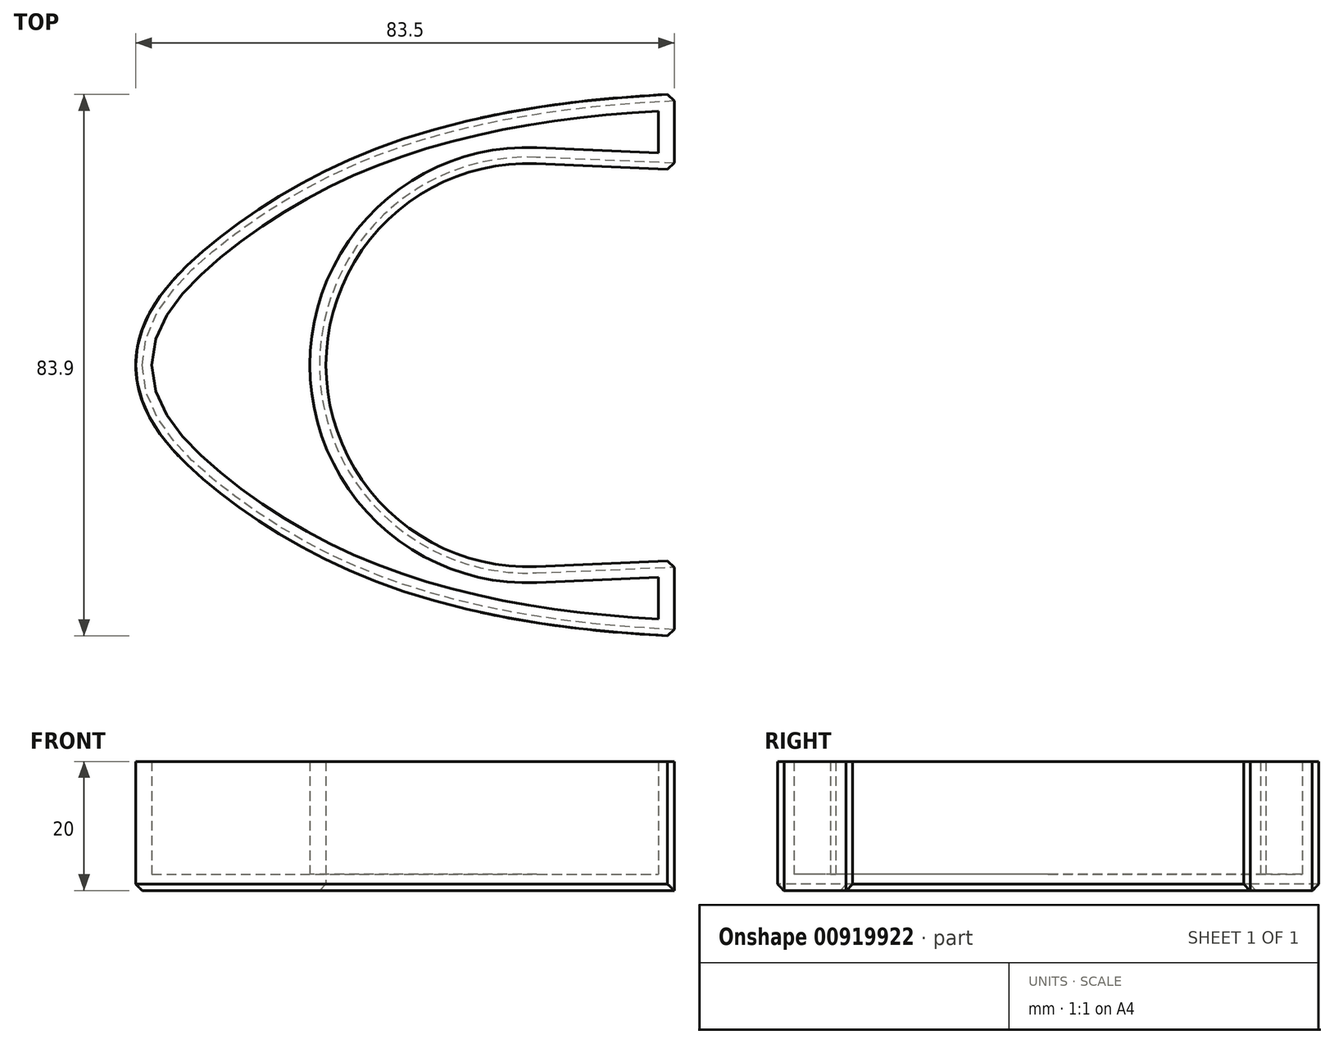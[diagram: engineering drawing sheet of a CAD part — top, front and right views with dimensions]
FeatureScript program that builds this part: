
annotation { "Feature Type Name" : "Feature", "Feature Type Description" : "" }
export const myFeature = defineFeature(function(context is Context, id is Id, definition is map)
    precondition{}
    {
        {
            var Q0;
            Q0=qCreatedBy(makeId("Top.planeOp"),FACE);
            var sketch = newSketch(context, id + "F0", { "sketchPlane" : qUnion([Q0])});
            skCircle(sketch, "E0", {"center": v(0, 0) * mm, "radius": 31.25 * mm});
            skLineSegment(sketch, "E1", {"start": v(22.75, 46.58) * mm, "end": v(22.75, -55.17) * mm, "construction": true});
            skLineSegment(sketch, "E2", {"start": v(1.34, 31.22) * mm, "end": v(22.75, 30.3) * mm});
            skLineSegment(sketch, "E3", {"start": v(1.34, -31.22) * mm, "end": v(22.75, -30.3) * mm});
            skPoint(sketch, "E4", {"position": v(22.75, 0) * mm});
            skFitSpline(sketch, "E5", {"points": [v(-60.75, 0) * mm, v(-45.42, 21.52) * mm, v(22.75, 42) * mm], "startDerivative": vector(0, 66.7) * mm, "endDerivative": vector(171.08, 7.64) * mm});
            skFitSpline(sketch, "E6", {"points": [v(-60.75, 0) * mm, v(-45.42, -21.52) * mm, v(22.75, -42) * mm], "startDerivative": vector(0, -66.7) * mm, "endDerivative": vector(171.08, -7.64) * mm});
            skLineSegment(sketch, "E7", {"start": v(22.75, -30.3) * mm, "end": v(22.75, -42) * mm});
            skLineSegment(sketch, "E8", {"start": v(22.75, 42) * mm, "end": v(22.75, 30.3) * mm});
            skPoint(sketch, "E9", {"position": v(-45.42, 0) * mm});
            skPoint(sketch, "E10", {"position": v(-12.69, 0) * mm});
            skLineSegment(sketch, "E11", {"start": v(-31.25, 0) * mm, "end": v(-31.25, 30.85) * mm, "construction": true});
            skSolve(sketch);
        }
        {
            var Q0;
            {var subQ1=sQuery(id+"F0.wireOp",EDGE,"E2");Q0=makeQuery(id+"F0.imprint","IMPRINT",FACE,{"disambiguationData":[TD([[makeQuery(id+"F0.imprint","IMPRINT",EDGE,{"derivedFrom":subQ1}),1.0]])]});}
            extrude(context, id + "F1", {"entities" : qUnion([Q0]), "depth" : 20 * mm, "offsetDistance" : 25 * mm});
        }
        {
            var Q0;
            Q0=makeQuery(id+"F1.opExtrude","CAP_FACE",FACE,{"disambiguationData":[OSD([sQuery(id+"F0.wireOp",EDGE,"E0"),sQuery(id+"F0.wireOp",EDGE,"E2"),sQuery(id+"F0.wireOp",EDGE,"E3"),sQuery(id+"F0.wireOp",EDGE,"E5"),sQuery(id+"F0.wireOp",EDGE,"E6"),sQuery(id+"F0.wireOp",EDGE,"E7"),sQuery(id+"F0.wireOp",EDGE,"E8")])],"isStart":false});
            shell(context, id + "F2", {"entities" : qUnion([Q0]), "thickness" : 2.5 * mm});
        }
        {
            var Q0;
            Q0=makeQuery(id+"F1.opExtrude","SWEPT_EDGE",EDGE,{"disambiguationData":[OSD([sQuery(id+"F0.wireOp",EDGE,"E6"),sQuery(id+"F0.wireOp",EDGE,"E7")])]});
            var Q1;
            Q1=makeQuery(id+"F1.opExtrude","SWEPT_EDGE",EDGE,{"disambiguationData":[OSD([sQuery(id+"F0.wireOp",EDGE,"E2"),sQuery(id+"F0.wireOp",EDGE,"E8")])]});
            var Q2;
            Q2=makeQuery(id+"F1.opExtrude","SWEPT_EDGE",EDGE,{"disambiguationData":[OSD([sQuery(id+"F0.wireOp",EDGE,"E5"),sQuery(id+"F0.wireOp",EDGE,"E8")])]});
            var Q3;
            Q3=makeQuery(id+"F1.opExtrude","SWEPT_EDGE",EDGE,{"disambiguationData":[OSD([sQuery(id+"F0.wireOp",EDGE,"E3"),sQuery(id+"F0.wireOp",EDGE,"E7")])]});
            var Q4;
            Q4=makeQuery(id+"F1.opExtrude","CAP_EDGE",EDGE,{"disambiguationData":[OSD([sQuery(id+"F0.wireOp",EDGE,"E6")])],"isStart":true});
            var Q5;
            Q5=makeQuery(id+"F1.opExtrude","CAP_EDGE",EDGE,{"disambiguationData":[OSD([sQuery(id+"F0.wireOp",EDGE,"E0")])],"isStart":true});
            chamfer(context, id + "F3", {"entities" : qUnion([Q0, Q1, Q2, Q3, Q4, Q5]), "width" : 1 * mm, "tangentPropagation" : true});
        }
    });
